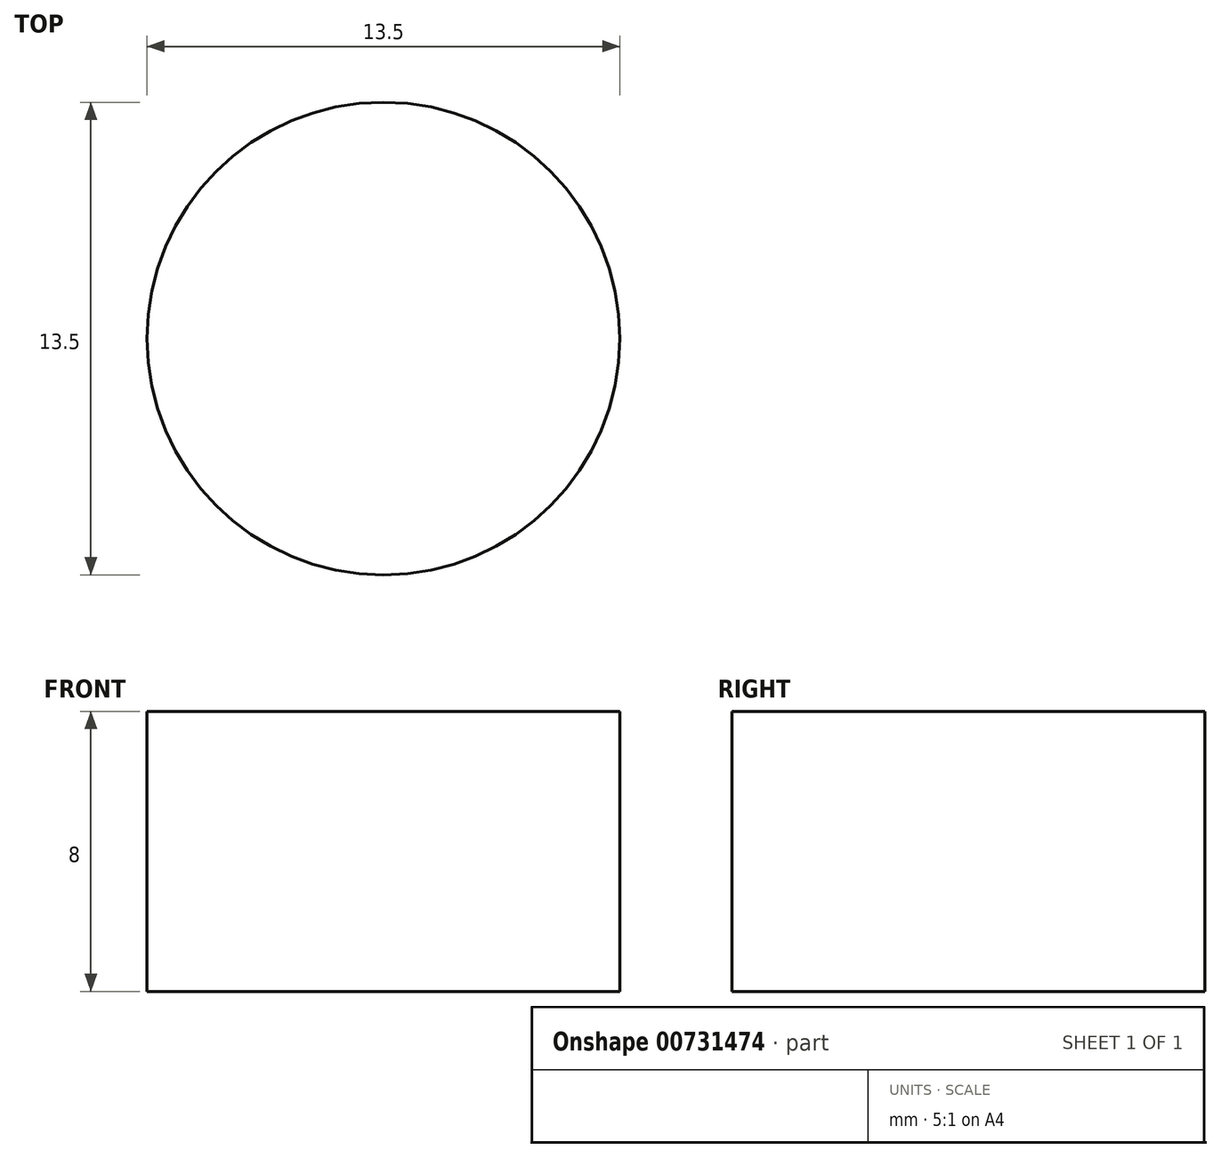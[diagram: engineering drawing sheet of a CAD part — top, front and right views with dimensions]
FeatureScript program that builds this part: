
annotation { "Feature Type Name" : "Feature", "Feature Type Description" : "" }
export const myFeature = defineFeature(function(context is Context, id is Id, definition is map)
    precondition{}
    {
        {
            var Q0;
            Q0=qCreatedBy(makeId("Top.planeOp"),FACE);
            var sketch = newSketch(context, id + "F0", { "sketchPlane" : qUnion([Q0])});
            skCircle(sketch, "E0", {"center": v(0, 0) * mm, "radius": 6.75 * mm});
            skSolve(sketch);
        }
        {
            var Q0;
            Q0=makeQuery(id+"F0.imprint","IMPRINT",FACE,{"disambiguationData":[TD([[makeQuery(id+"F0.imprint","IMPRINT",EDGE,{"derivedFrom":sQuery(id+"F0.wireOp",EDGE,"E0")}),1.0]])]});
            extrude(context, id + "F1", {"entities" : qUnion([Q0]), "depth" : 8 * mm, "offsetDistance" : 25 * mm});
        }
        {
            var Q0;
            Q0=qCreatedBy(makeId("Top.planeOp"),FACE);
            var sketch = newSketch(context, id + "F2", { "sketchPlane" : qUnion([Q0])});
            skCircle(sketch, "E1", {"center": v(0, 0) * mm, "radius": 1.5 * mm});
            skCircle(sketch, "E2", {"center": v(0, 0) * mm, "radius": 5.5 * mm});
            skLineSegment(sketch, "E3", {"start": v(0, 5.5) * mm, "end": v(0, 1.5) * mm});
            skLineSegment(sketch, "E4", {"start": v(-0.69, 1.33) * mm, "end": v(-2.38, 4.96) * mm});
            skSolve(sketch);
        }
    });
